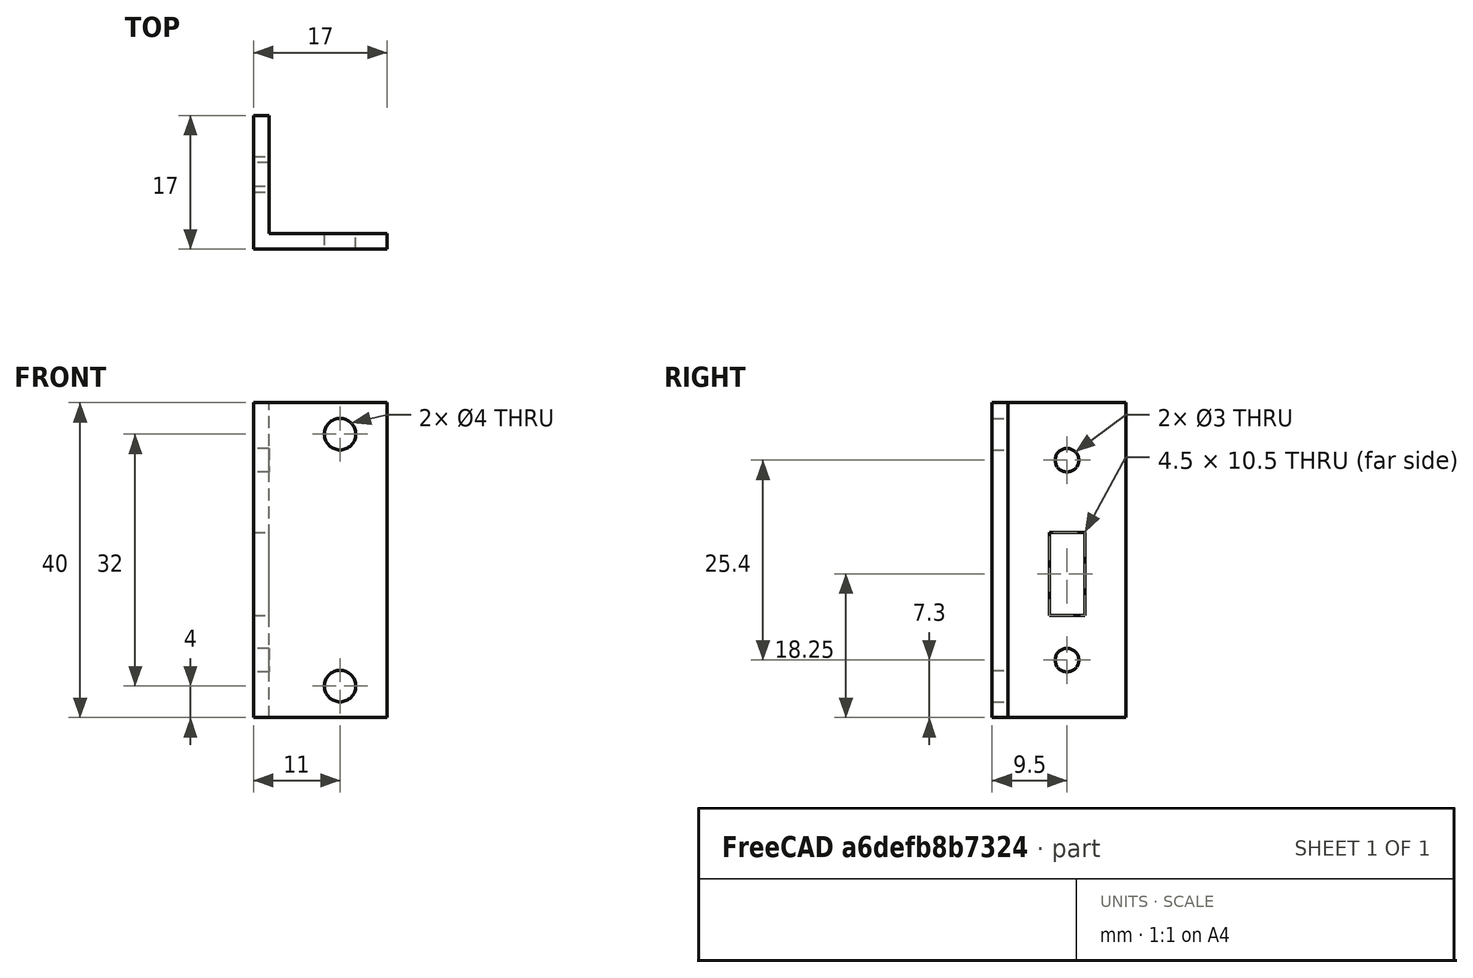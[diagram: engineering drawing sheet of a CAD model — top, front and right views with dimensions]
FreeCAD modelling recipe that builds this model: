
FCSTD DOCUMENT  (FreeCAD 0.20R)
Label: Support_interrupteur_V1
License: All rights reserved
LicenseURL: http://en.wikipedia.org/wiki/All_rights_reserved
objects: Sketcher::SketchObject×3, PartDesign::Pocket×2, PartDesign::Pad×1, PartDesign::Body×1, Mesh::Feature×1
note: 10 computed .brp shape members not serialized (recipe doc carries the construction recipe); baked Part::Feature solids carry a one-line shape summary decoded from their .brp

FEATURE [Sketcher::SketchObject] Sketch
  FullyConstrained = true
  MapMode = 5
  Support = -> [XY_Plane]
  sketch-geometry (6):
    g0: LineSegment StartX=0 StartY=15 StartZ=0 EndX=0 EndY=0 EndZ=0
    g1: LineSegment StartX=0 StartY=0 StartZ=0 EndX=15 EndY=0 EndZ=0
    g2: LineSegment StartX=15 StartY=0 StartZ=0 EndX=15 EndY=-2 EndZ=0
    g3: LineSegment StartX=15 StartY=-2 StartZ=0 EndX=-2 EndY=-2 EndZ=0
    g4: LineSegment StartX=-2 StartY=-2 StartZ=0 EndX=-2 EndY=15 EndZ=0
    g5: LineSegment StartX=-2 StartY=15 StartZ=0 EndX=0 EndY=15 EndZ=0
  constraints (17):
    c: PointOnObject(g0,g-2)
    c: Coincident(g0,g-1)
    c: Coincident(g0,g1)
    c: PointOnObject(g1,g-1)
    c: Coincident(g1,g2)
    c: Vertical(g2)
    c: Coincident(g2,g3)
    c: Horizontal(g3)
    c: Coincident(g3,g4)
    c: Vertical(g4)
    c: Coincident(g4,g5)
    c: Coincident(g5,g0)
    c: Horizontal(g5)
    c: DistanceX(g5,g5) = 2
    c: DistanceY(g2,g2) = 2
    c: DistanceX(g1,g1) = 15
    c: DistanceY(g0,g0) = 15
FEATURE [PartDesign::Pad] Pad
  Direction = (0,0,1)
  Length = 40
  Length2 = 100
  Profile = -> Sketch
  Type = 0
FEATURE [Sketcher::SketchObject] Sketch001
  FullyConstrained = true
  MapMode = 5
  Placement = pos=(-2,0,0) rot=(0.57735,-0.57735,-0.57735;2.0944rad)
  Support = -> [Pad]
  sketch-geometry (6):
    g0: Circle CenterX=-7.5 CenterY=32.7 CenterZ=0 NormalX=0 NormalY=0 NormalZ=1 AngleXU=0 Radius=1.5
    g1: Circle CenterX=-7.5 CenterY=7.3 CenterZ=0 NormalX=0 NormalY=0 NormalZ=1 AngleXU=0 Radius=1.5
    g2: LineSegment StartX=-9.75 StartY=23.5 StartZ=0 EndX=-5.25 EndY=23.5 EndZ=0
    g3: LineSegment StartX=-5.25 StartY=23.5 StartZ=0 EndX=-5.25 EndY=13 EndZ=0
    g4: LineSegment StartX=-5.25 StartY=13 StartZ=0 EndX=-9.75 EndY=13 EndZ=0
    g5: LineSegment StartX=-9.75 StartY=13 StartZ=0 EndX=-9.75 EndY=23.5 EndZ=0
  constraints (18):
    c: DistanceX(g-2,g0) = -7.5
    c: DistanceX(g-2,g1) = -7.5
    c: Distance(g0,g1) = 25.4
    c: Radius(g0) = 1.5
    c: Equal(g0,g1)
    c: Coincident(g2,g3)
    c: Coincident(g3,g4)
    c: Coincident(g4,g5)
    c: Coincident(g5,g2)
    c: Horizontal(g2)
    c: Horizontal(g4)
    c: Vertical(g3)
    c: Vertical(g5)
    c: DistanceX(g4,g4) = 4.5
    c: DistanceY(g5,g5) = 10.5
    c: DistanceX(g-2,g3) = -5.25
    c: DistanceY(g-1,g3) = 13
    c: DistanceY(g-1,g1) = 7.3
FEATURE [PartDesign::Pocket] Pocket
  BaseFeature = -> Pad
  Length = 5
  Length2 = 100
  Profile = -> Sketch001
  Type = 0
FEATURE [Sketcher::SketchObject] Sketch002
  ExternalGeometry = -> [Pocket]
  FullyConstrained = true
  MapMode = 5
  Placement = pos=(0,0,0) rot=(0,0.707107,0.707107;3.14159rad)
  Support = -> [Pocket]
  sketch-geometry (2):
    g0: Circle CenterX=-9 CenterY=36 CenterZ=0 NormalX=0 NormalY=0 NormalZ=1 AngleXU=0 Radius=2
    g1: Circle CenterX=-9 CenterY=4 CenterZ=0 NormalX=0 NormalY=0 NormalZ=1 AngleXU=0 Radius=2
  constraints (6):
    c: Radius(g0) = 2
    c: Equal(g0,g1)
    c: DistanceY(g-1,g1) = 4
    c: Distance(g0,g-3) = 4
    c: Distance(g0,g-4) = 6
    c: Distance(g1,g-4) = 6
FEATURE [PartDesign::Pocket] Pocket001
  BaseFeature = -> Pocket
  Length = 5
  Length2 = 100
  Profile = -> Sketch002
  Type = 0
FEATURE [PartDesign::Body] Body  label="Support_unterrupteur"
  Group = -> [Sketch,Pad,Sketch001,Pocket,Sketch002,Pocket001]
  Origin = -> Origin
  Tip = -> Pocket001
FEATURE [Mesh::Feature] Mesh  label="Support_unterrupteur (Meshed)"
